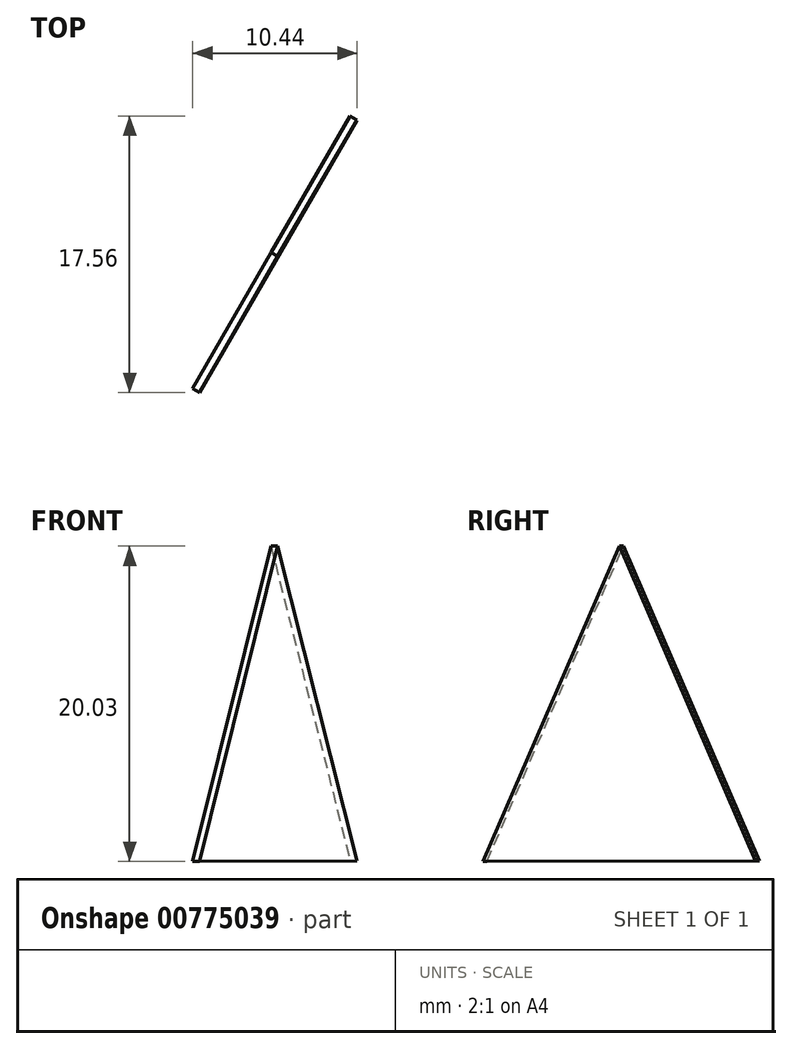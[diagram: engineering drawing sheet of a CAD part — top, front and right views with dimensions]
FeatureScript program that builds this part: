
annotation { "Feature Type Name" : "Feature", "Feature Type Description" : "" }
export const myFeature = defineFeature(function(context is Context, id is Id, definition is map)
    precondition{}
    {
        {
            var Q0;
            Q0=qCreatedBy(makeId("Top.planeOp"),FACE);
            var sketch = newSketch(context, id + "F0", { "sketchPlane" : qUnion([Q0])});
            skCircle(sketch, "E0.cCircle", {"center": v(0, 0) * mm, "radius": 17.32 * mm, "construction": true});
            skLineSegment(sketch, "E0.0", {"start": v(20, 0) * mm, "end": v(10, -17.32) * mm});
            skLineSegment(sketch, "E0.1", {"start": v(10, -17.32) * mm, "end": v(-10, -17.32) * mm});
            skLineSegment(sketch, "E0.2", {"start": v(-10, -17.32) * mm, "end": v(-20, 0) * mm});
            skLineSegment(sketch, "E0.3", {"start": v(-20, 0) * mm, "end": v(-10, 17.32) * mm});
            skLineSegment(sketch, "E0.4", {"start": v(-10, 17.32) * mm, "end": v(10, 17.32) * mm});
            skLineSegment(sketch, "E0.5", {"start": v(10, 17.32) * mm, "end": v(20, 0) * mm});
            skPoint(sketch, "E0.0.midPoint", {"position": v(15, -8.67) * mm});
            skSolve(sketch);
        }
        {
            var Q0;
            Q0=qCreatedBy(makeId("Top.planeOp"),FACE);
            cPlane(context, id + "F1", {"entities" : qUnion([Q0]), "cplaneType" : CPlaneType.OFFSET, "offset" : 20 * mm, "width" : 150 * mm, "height" : 150 * mm});
        }
        {
            var Q0;
            Q0=qCreatedBy(id+"F1.planeOp",FACE);
            var sketch = newSketch(context, id + "F2", { "sketchPlane" : qUnion([Q0])});
            skCircle(sketch, "E1.cCircle", {"center": v(0, 0) * mm, "radius": 15.03 * mm, "construction": true});
            skLineSegment(sketch, "E1.0", {"start": v(-0.06, 17.35) * mm, "end": v(15, 8.73) * mm});
            skLineSegment(sketch, "E1.1", {"start": v(15, 8.73) * mm, "end": v(15.06, -8.63) * mm});
            skLineSegment(sketch, "E1.2", {"start": v(15.06, -8.63) * mm, "end": v(0.06, -17.35) * mm});
            skLineSegment(sketch, "E1.3", {"start": v(0.06, -17.35) * mm, "end": v(-15, -8.73) * mm});
            skLineSegment(sketch, "E1.4", {"start": v(-15, -8.73) * mm, "end": v(-15.06, 8.63) * mm});
            skLineSegment(sketch, "E1.5", {"start": v(-15.06, 8.63) * mm, "end": v(-0.06, 17.35) * mm});
            skPoint(sketch, "E1.0.midPoint", {"position": v(7.47, 13.04) * mm});
            skSolve(sketch);
        }
        {
            var Q0;
            Q0=sQuery(id+"F0.wireOp",VERTEX,"E0.3.end");
            var Q1;
            Q1=sQuery(id+"F2.wireOp",VERTEX,"E1.4.end");
            var Q2;
            Q2=sQuery(id+"F0.wireOp",VERTEX,"E0.2.end");
            cPlane(context, id + "F3", {"entities" : qUnion([Q0, Q1, Q2]), "cplaneType" : CPlaneType.THREE_POINT, "offset" : 25 * mm, "width" : 150 * mm, "height" : 150 * mm});
        }
        {
            var Q0;
            Q0=qCreatedBy(id+"F3.planeOp",FACE);
            var sketch = newSketch(context, id + "F4", { "sketchPlane" : qUnion([Q0])});
            skLineSegment(sketch, "E2", {"start": v(0, 20.02) * mm, "end": v(-10, 0) * mm});
            skLineSegment(sketch, "E3", {"start": v(-10, 0) * mm, "end": v(10, 0) * mm});
            skLineSegment(sketch, "E4", {"start": v(10, 0) * mm, "end": v(0, 20.02) * mm});
            skSolve(sketch);
        }
        {
            var Q0;
            Q0 = qSketchRegion(id + "F4", true);
            extrude(context, id + "F5", {"entities" : qUnion([Q0]), "oppositeDirection" : true, "depth" : .5 * mm, "offsetDistance" : 25 * mm});
        }
    });
